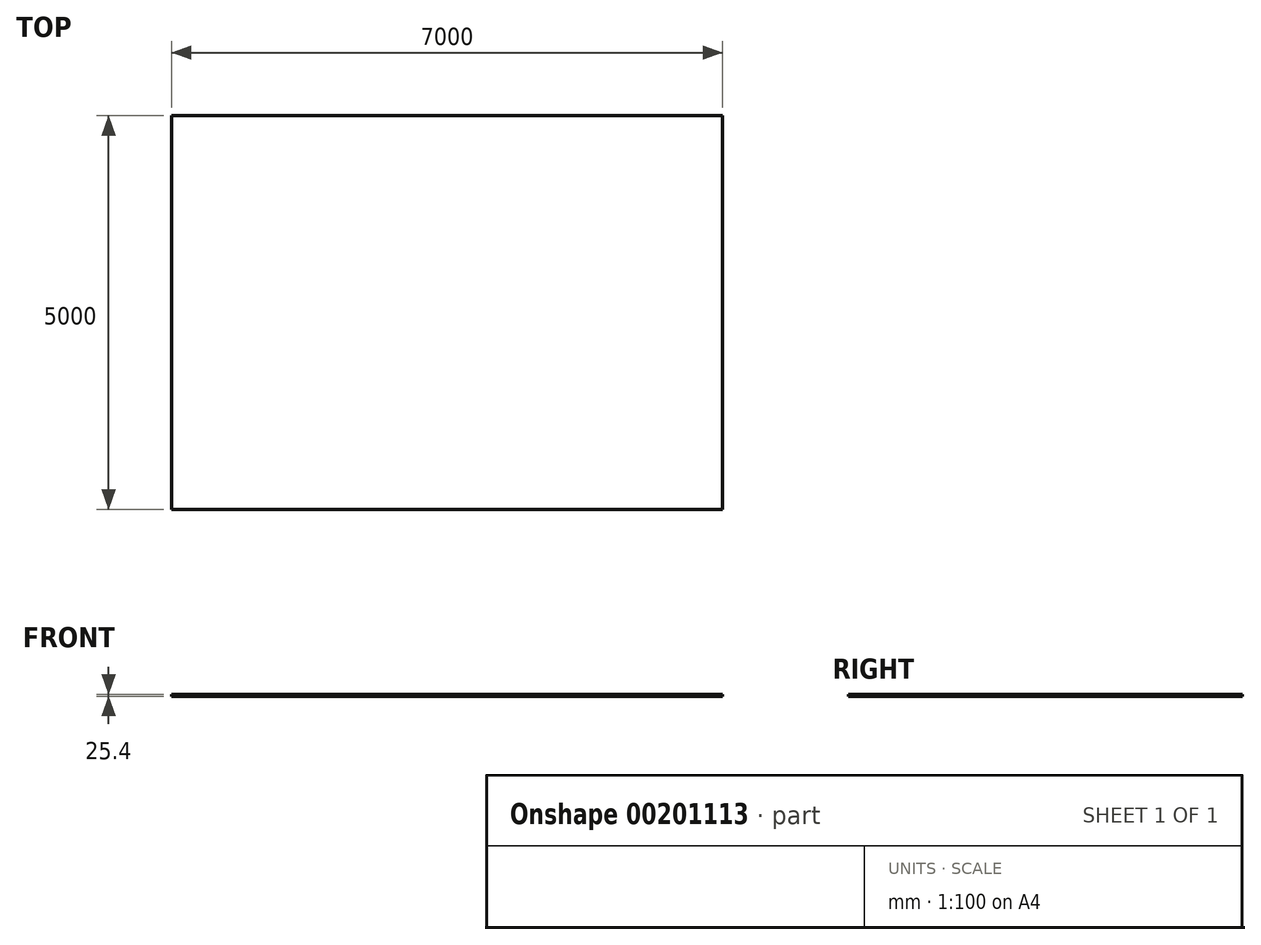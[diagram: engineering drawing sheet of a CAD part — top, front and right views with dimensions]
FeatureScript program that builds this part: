
annotation { "Feature Type Name" : "Feature", "Feature Type Description" : "" }
export const myFeature = defineFeature(function(context is Context, id is Id, definition is map)
    precondition{}
    {
        {
            var Q0;
            Q0=qCreatedBy(makeId("Top.planeOp"),FACE);
            var sketch = newSketch(context, id + "F0", { "sketchPlane" : qUnion([Q0])});
            skLineSegment(sketch, "E0.bottom", {"start": v(-3500, -2500) * mm, "end": v(3500, -2500) * mm});
            skLineSegment(sketch, "E0.top", {"start": v(-3500, 2500) * mm, "end": v(3500, 2500) * mm});
            skLineSegment(sketch, "E0.left", {"start": v(-3500, -2500) * mm, "end": v(-3500, 2500) * mm});
            skLineSegment(sketch, "E0.right", {"start": v(3500, -2500) * mm, "end": v(3500, 2500) * mm});
            skPoint(sketch, "E0.middle", {"position": v(0, 0) * mm});
            skSolve(sketch);
        }
        {
            var Q0;
            Q0 = qSketchRegion(id + "F0", true);
            extrude(context, id + "F1", {"entities" : qUnion([Q0]), "oppositeDirection" : true, "depth" : 25.4 * mm});
        }
    });
